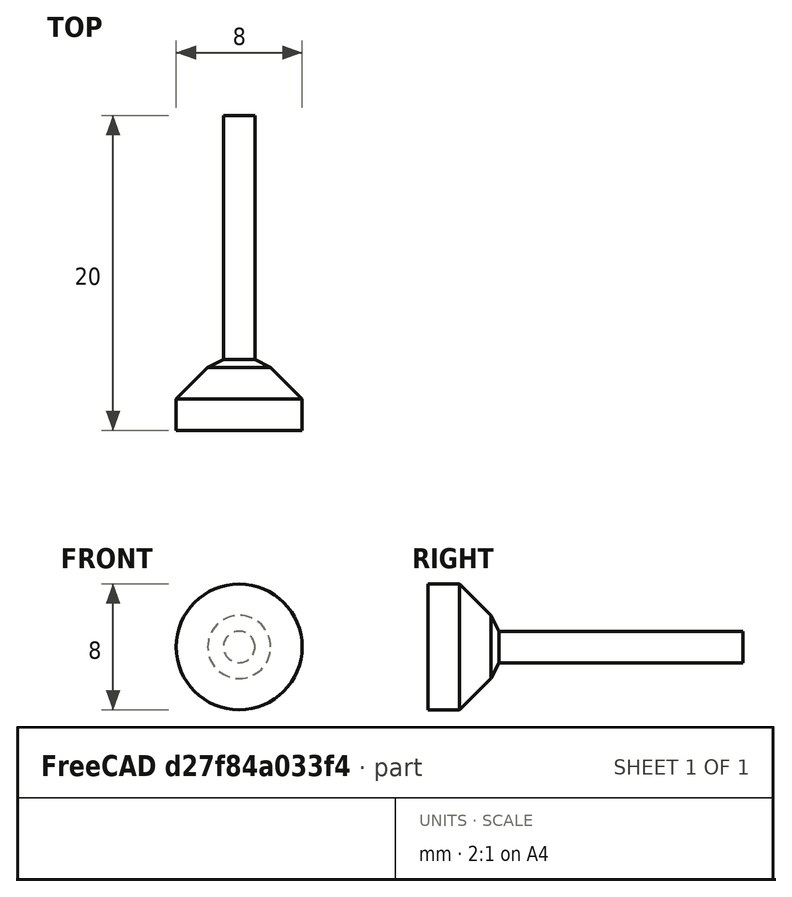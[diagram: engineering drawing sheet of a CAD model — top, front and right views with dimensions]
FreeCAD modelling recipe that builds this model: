
FCSTD DOCUMENT  (FreeCAD 0.17R8715 (Git))
Label: conic_valve
License: CreativeCommons Attribution
LicenseURL: http://creativecommons.org/licenses/by/4.0/
objects: Sketcher::SketchObject×1, PartDesign::Revolution×1, PartDesign::Body×1
note: 4 computed .brp shape members not serialized (recipe doc carries the construction recipe); baked Part::Feature solids carry a one-line shape summary decoded from their .brp

FEATURE [Sketcher::SketchObject] Sketch
  MapMode = 5
  Support = -> [XY_Plane]
  sketch-geometry (8):
    g0: LineSegment StartX=0 StartY=0 StartZ=0 EndX=-4 EndY=0 EndZ=0
    g1: LineSegment StartX=-4 StartY=0 StartZ=0 EndX=-4 EndY=2 EndZ=0
    g2: LineSegment StartX=-4 StartY=2 StartZ=0 EndX=-2 EndY=4 EndZ=0
    g3: LineSegment StartX=-2 StartY=4 StartZ=0 EndX=-1 EndY=4.5 EndZ=0
    g4: LineSegment StartX=-1 StartY=4.5 StartZ=0 EndX=-1 EndY=20 EndZ=0
    g5: LineSegment StartX=-1 StartY=20 StartZ=0 EndX=0 EndY=20 EndZ=0
    g6: LineSegment StartX=0 StartY=20 StartZ=0 EndX=0 EndY=0 EndZ=0
    g7: LineSegment [constr] StartX=0 StartY=0 StartZ=0 EndX=0 EndY=25 EndZ=0
  constraints (23):
    c: Coincident(g-1,g0)
    c: Coincident(g0,g1)
    c: Coincident(g1,g2)
    c: Coincident(g2,g3)
    c: Coincident(g3,g4)
    c: Vertical(g4)
    c: Coincident(g4,g5)
    c: Horizontal(g5)
    c: Coincident(g5,g6)
    c: Coincident(g6,g0)
    c: Vertical(g6)
    c: Coincident(g7,g-1)
    c: Vertical(g7)
    c: DistanceX(g0,g-1) = 4
    c: DistanceX(g1,g-1) = 4
    c: DistanceY(g-1,g1) = 2
    c: DistanceY(g-1,g5) = 20
    c: DistanceX(g2,g-1) = 2
    c: DistanceY(g1,g2) = 2
    c: DistanceY(g2,g3) = 0.5
    c: DistanceX(g3,g-1) = 1
    c: Horizontal(g0)
    c: DistanceY(g7) = 25
FEATURE [PartDesign::Revolution] Revolution
  Angle = 360
  Axis = (0,1,0)
  Base = (0,0,0)
  Profile = -> Sketch
  ReferenceAxis = -> Sketch [V_Axis]
FEATURE [PartDesign::Body] Body
  Model = -> [Sketch,Revolution]
  Origin = -> BodyOrigin
  Tip = -> Revolution
